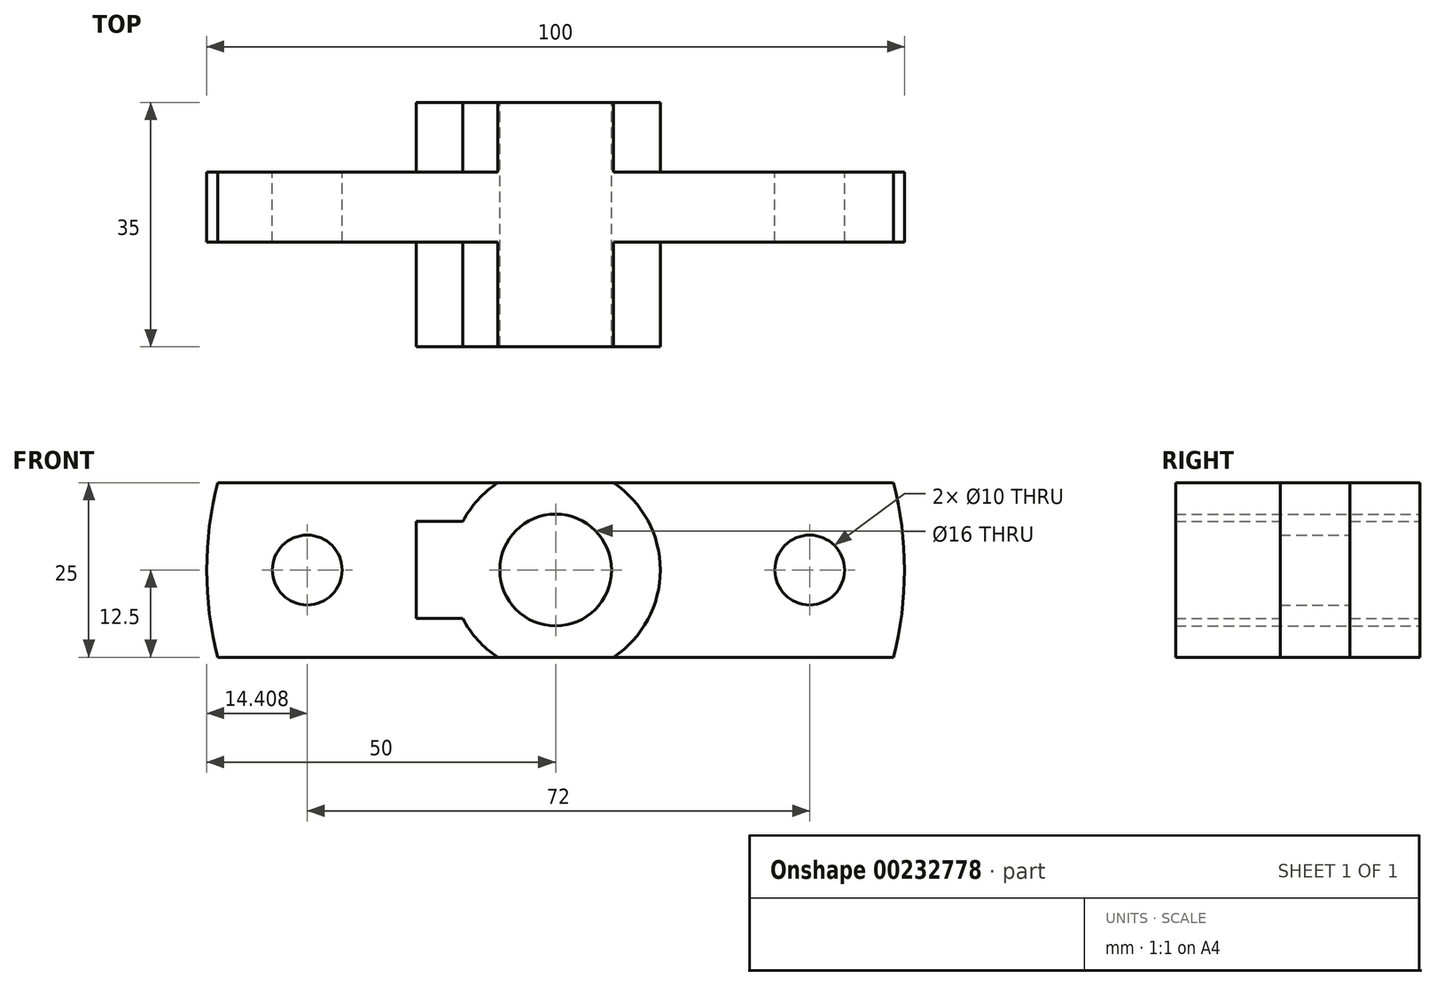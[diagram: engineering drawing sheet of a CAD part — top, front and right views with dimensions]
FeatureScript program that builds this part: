
annotation { "Feature Type Name" : "Feature", "Feature Type Description" : "" }
export const myFeature = defineFeature(function(context is Context, id is Id, definition is map)
    precondition{}
    {
        {
            var Q0;
            Q0=qCreatedBy(makeId("Front.planeOp"),FACE);
            var sketch = newSketch(context, id + "F0", { "sketchPlane" : qUnion([Q0])});
            skCircle(sketch, "E0", {"center": v(0, 0) * mm, "radius": 8 * mm});
            skArc(sketch, "E1", {"start": v(8.3, -12.5) * mm, "mid": v(15, 0) * mm, "end": v(8.3, 12.5) * mm});
            skArc(sketch, "E2", {"start": v(-48.41, 12.5) * mm, "mid": v(-50, 0) * mm, "end": v(-48.41, -12.5) * mm});
            skLineSegment(sketch, "E3.bottom", {"start": v(-48.41, 12.5) * mm, "end": v(48.41, 12.5) * mm});
            skLineSegment(sketch, "E3.top", {"start": v(-48.41, -12.5) * mm, "end": v(48.41, -12.5) * mm});
            skArc(sketch, "E4.trimOffspring", {"start": v(48.41, -12.5) * mm, "mid": v(50, 0) * mm, "end": v(48.41, 12.5) * mm});
            skArc(sketch, "E5.trimOffspring", {"start": v(-8.3, 12.5) * mm, "mid": v(-11.14, 10.04) * mm, "end": v(-13.3, 6.95) * mm});
            skPoint(sketch, "E6.orphan", {"position": v(-66.05, 12.5) * mm});
            skPoint(sketch, "E7.orphan", {"position": v(-66.05, -12.5) * mm});
            skPoint(sketch, "E3.right.end.orphan", {"position": v(66.05, -12.5) * mm});
            skPoint(sketch, "E3.right.start.orphan", {"position": v(66.05, 12.5) * mm});
            skCircle(sketch, "E8", {"center": v(-35.6, 0) * mm, "radius": 5 * mm});
            skCircle(sketch, "E9", {"center": v(36.4, 0) * mm, "radius": 5 * mm});
            skLineSegment(sketch, "E10.bottom", {"start": v(-20, -6.95) * mm, "end": v(-13.3, -6.95) * mm});
            skLineSegment(sketch, "E10.top", {"start": v(-20, 6.95) * mm, "end": v(-13.3, 6.95) * mm});
            skLineSegment(sketch, "E10.right", {"start": v(-20, 6.95) * mm, "end": v(-20, -6.95) * mm});
            skPoint(sketch, "E10.middle", {"position": v(-15, 0) * mm});
            skPoint(sketch, "E10.left.end.orphan", {"position": v(-10, 6.95) * mm});
            skArc(sketch, "E11.trimOffspring", {"start": v(-13.3, -6.95) * mm, "mid": v(-11.14, -10.04) * mm, "end": v(-8.3, -12.5) * mm});
            skPoint(sketch, "E12.orphan", {"position": v(-10, -6.95) * mm});
            skSolve(sketch);
        }
        {
            var Q0;
            Q0=makeQuery(id+"F0.imprint","IMPRINT",FACE,{"disambiguationData":[TD([[makeQuery(id+"F0.imprint","IMPRINT",EDGE,{"derivedFrom":sQuery(id+"F0.wireOp",EDGE,"E0")}),-1.0]])]});
            extrude(context, id + "F1", {"entities" : qUnion([Q0]), "depth" : 25 * mm, "hasSecondDirection" : true, "secondDirectionOppositeDirection" : true, "secondDirectionDepth" : 10 * mm});
        }
        {
            var Q0;
            {var subQ2=sQuery(id+"F0.wireOp",EDGE,"E1");Q0=makeQuery(id+"F0.imprint","IMPRINT",FACE,{"disambiguationData":[TD([[makeQuery(id+"F0.imprint","IMPRINT",EDGE,{"derivedFrom":subQ2}),-1.0]])]});}
            var Q1;
            {var subQ2=sQuery(id+"F0.wireOp",EDGE,"E2");Q1=makeQuery(id+"F0.imprint","IMPRINT",FACE,{"disambiguationData":[TD([[makeQuery(id+"F0.imprint","IMPRINT",EDGE,{"derivedFrom":subQ2}),1.0]])]});}
            extrude(context, id + "F2", {"entities" : qUnion([Q0, Q1]), "operationType" : NewBodyOperationType.ADD, "depth" : 10 * mm});
        }
    });
